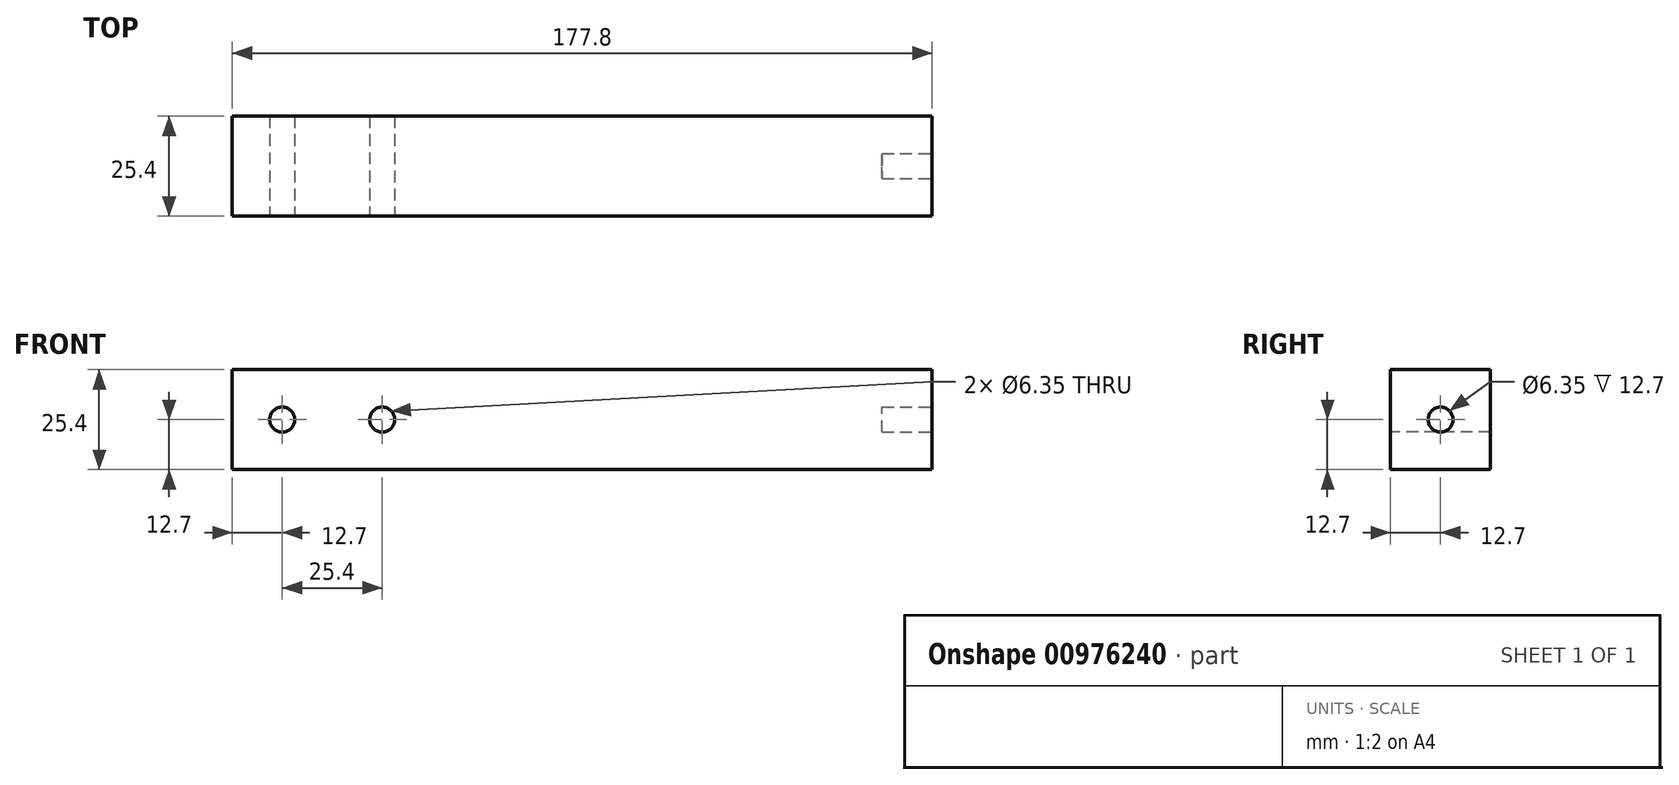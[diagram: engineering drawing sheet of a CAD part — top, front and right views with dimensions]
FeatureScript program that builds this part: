
annotation { "Feature Type Name" : "Feature", "Feature Type Description" : "" }
export const myFeature = defineFeature(function(context is Context, id is Id, definition is map)
    precondition{}
    {
        {
            var Q0;
            Q0=qCreatedBy(makeId("Top.planeOp"),FACE);
            var sketch = newSketch(context, id + "F0", { "sketchPlane" : qUnion([Q0])});
            skLineSegment(sketch, "E0.bottom", {"start": v(-88.9, 12.7) * mm, "end": v(88.9, 12.7) * mm});
            skLineSegment(sketch, "E0.top", {"start": v(-88.9, -12.7) * mm, "end": v(88.9, -12.7) * mm});
            skLineSegment(sketch, "E0.left", {"start": v(-88.9, 12.7) * mm, "end": v(-88.9, -12.7) * mm});
            skLineSegment(sketch, "E0.right", {"start": v(88.9, 12.7) * mm, "end": v(88.9, -12.7) * mm});
            skPoint(sketch, "E0.middle", {"position": v(0, 0) * mm});
            skSolve(sketch);
        }
        {
            var Q0;
            Q0=makeQuery(id+"F0.imprint","IMPRINT",FACE,{"disambiguationData":[TD([[makeQuery(id+"F0.imprint","IMPRINT",EDGE,{"derivedFrom":sQuery(id+"F0.wireOp",EDGE,"E0.bottom")}),-1.0]])]});
            extrude(context, id + "F1", {"entities" : qUnion([Q0]), "depth" : 25.4 * mm, "offsetDistance" : 25.4 * mm});
        }
        {
            var Q0;
            Q0=makeQuery(id+"F1.opExtrude","SWEPT_FACE",FACE,{"disambiguationData":[OSD([sQuery(id+"F0.wireOp",EDGE,"E0.top")])]});
            var sketch = newSketch(context, id + "F2", { "sketchPlane" : qUnion([Q0])});
            skCircle(sketch, "E1", {"center": v(-76.2, 12.7) * mm, "radius": 3.18 * mm});
            skCircle(sketch, "E2", {"center": v(-50.8, 12.7) * mm, "radius": 3.18 * mm});
            skSolve(sketch);
        }
        {
            var Q0;
            Q0=makeQuery(id+"F2.imprint","IMPRINT",FACE,{"disambiguationData":[TD([[makeQuery(id+"F2.imprint","IMPRINT",EDGE,{"derivedFrom":sQuery(id+"F2.wireOp",EDGE,"E1")}),1.0]])]});
            var Q1;
            Q1=makeQuery(id+"F2.imprint","IMPRINT",FACE,{"disambiguationData":[TD([[makeQuery(id+"F2.imprint","IMPRINT",EDGE,{"derivedFrom":sQuery(id+"F2.wireOp",EDGE,"E2")}),1.0]])]});
            extrude(context, id + "F3", {"entities" : qUnion([Q0, Q1]), "operationType" : NewBodyOperationType.REMOVE, "oppositeDirection" : true, "depth" : 25.4 * mm, "offsetDistance" : 25.4 * mm});
        }
        {
            var Q0;
            Q0=makeQuery(id+"F1.opExtrude","SWEPT_FACE",FACE,{"disambiguationData":[OSD([sQuery(id+"F0.wireOp",EDGE,"E0.right")])]});
            var sketch = newSketch(context, id + "F4", { "sketchPlane" : qUnion([Q0])});
            skCircle(sketch, "E3", {"center": v(0, 12.7) * mm, "radius": 3.18 * mm});
            skPoint(sketch, "E3.centerSnap0", {"position": v(-12.7, 12.7) * mm});
            skSolve(sketch);
        }
        {
            var Q0;
            Q0 = qSketchRegion(id + "F4", true);
            extrude(context, id + "F5", {"entities" : qUnion([Q0]), "operationType" : NewBodyOperationType.REMOVE, "oppositeDirection" : true, "depth" : 12.7 * mm, "offsetDistance" : 25.4 * mm});
        }
    });
